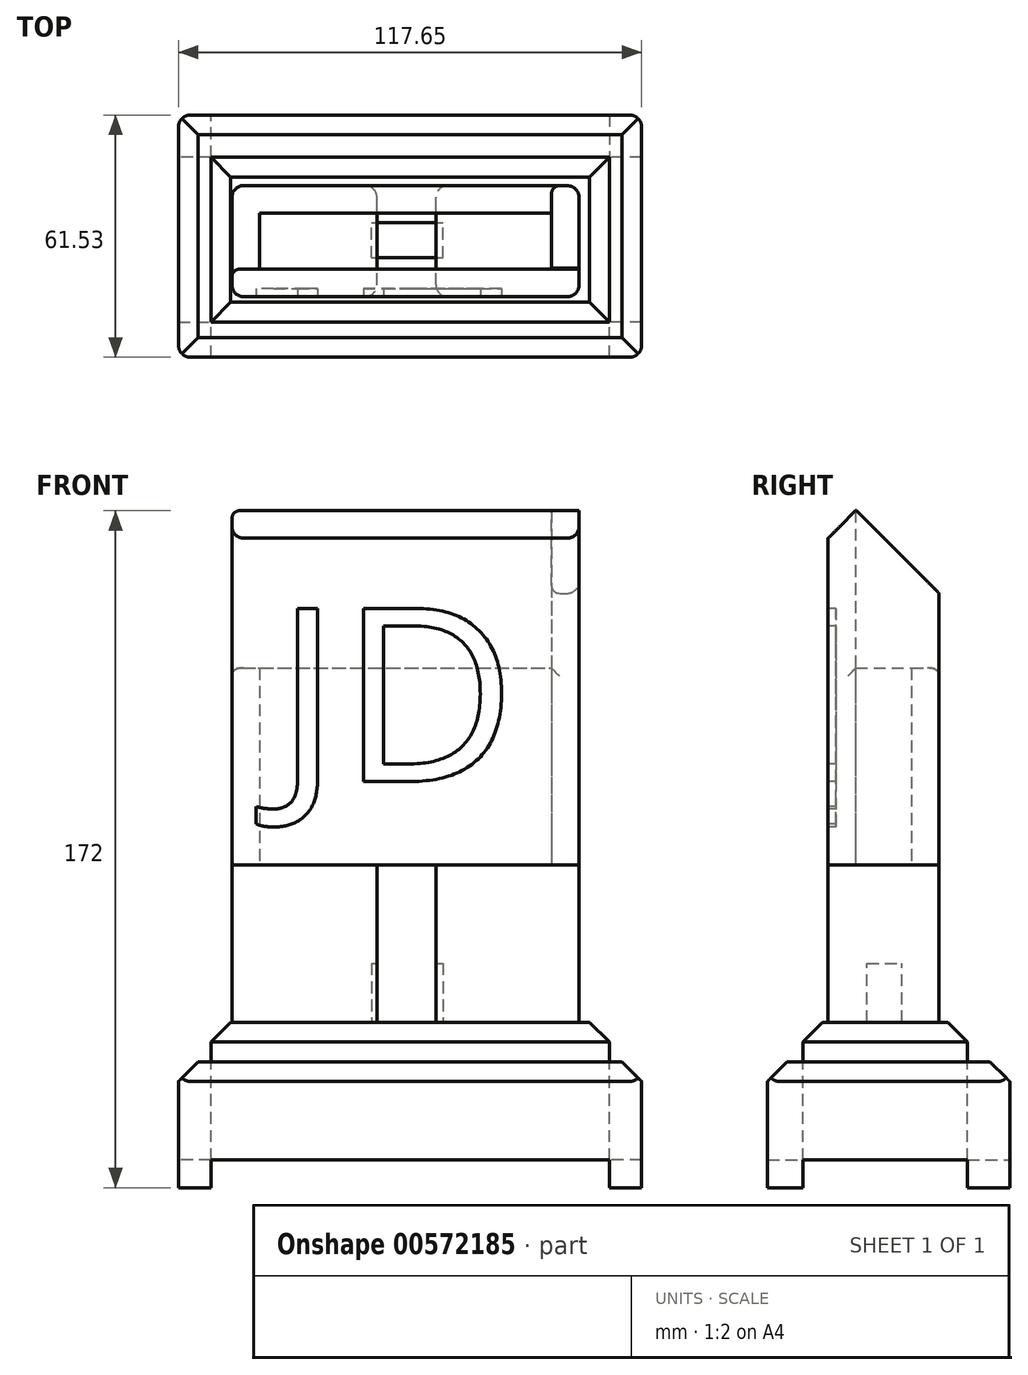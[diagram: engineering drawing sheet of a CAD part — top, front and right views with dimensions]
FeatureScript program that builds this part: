
annotation { "Feature Type Name" : "Feature", "Feature Type Description" : "" }
export const myFeature = defineFeature(function(context is Context, id is Id, definition is map)
    precondition{}
    {
        {
            var Q0;
            Q0=qCreatedBy(makeId("Top.planeOp"),FACE);
            var sketch = newSketch(context, id + "F0", { "sketchPlane" : qUnion([Q0])});
            skLineSegment(sketch, "E0.bottom", {"start": v(-33.87, 3.16) * mm, "end": v(33.23, 3.16) * mm});
            skLineSegment(sketch, "E0.top", {"start": v(-33.87, -3.94) * mm, "end": v(33.23, -3.94) * mm});
            skLineSegment(sketch, "E0.left", {"start": v(-33.87, 3.16) * mm, "end": v(-33.87, -3.94) * mm});
            skLineSegment(sketch, "E0.right", {"start": v(33.23, 3.16) * mm, "end": v(33.23, -3.94) * mm});
            skSolve(sketch);
        }
        {
            var Q0;
            Q0=makeQuery(id+"F0.imprint","IMPRINT",FACE,{"disambiguationData":[TD([[makeQuery(id+"F0.imprint","IMPRINT",EDGE,{"derivedFrom":sQuery(id+"F0.wireOp",EDGE,"E0.bottom")}),-1.0]])]});
            extrude(context, id + "F1", {"entities" : qUnion([Q0]), "depth" : 138.3 * mm, "offsetDistance" : 25 * mm});
        }
        {
            var Q0;
            Q0=qCreatedBy(makeId("Top.planeOp"),FACE);
            var sketch = newSketch(context, id + "F2", { "sketchPlane" : qUnion([Q0])});
            skLineSegment(sketch, "E1.bottom", {"start": v(-37.47, -7.59) * mm, "end": v(36.73, -7.59) * mm});
            skLineSegment(sketch, "E1.top", {"start": v(-37.47, 6.61) * mm, "end": v(36.73, 6.61) * mm});
            skLineSegment(sketch, "E1.left", {"start": v(-37.47, -7.59) * mm, "end": v(-37.47, 6.61) * mm});
            skLineSegment(sketch, "E1.right", {"start": v(36.73, -7.59) * mm, "end": v(36.73, 6.61) * mm});
            skLineSegment(sketch, "E2.0", {"start": v(-44.47, -14.59) * mm, "end": v(43.73, -14.59) * mm});
            skLineSegment(sketch, "E2.1", {"start": v(-44.47, -14.59) * mm, "end": v(-44.47, 13.61) * mm});
            skLineSegment(sketch, "E2.2", {"start": v(-44.47, 13.61) * mm, "end": v(43.73, 13.61) * mm});
            skLineSegment(sketch, "E2.3", {"start": v(43.73, -14.59) * mm, "end": v(43.73, 13.61) * mm});
            skSolve(sketch);
        }
        {
            var Q0;
            Q0=makeQuery(id+"F2.imprint","IMPRINT",FACE,{"disambiguationData":[TD([[makeQuery(id+"F2.imprint","IMPRINT",EDGE,{"derivedFrom":sQuery(id+"F2.wireOp",EDGE,"E1.bottom")}),-1.0]])]});
            extrude(context, id + "F3", {"entities" : qUnion([Q0]), "depth" : 50 * mm, "offsetDistance" : 25 * mm});
        }
        {
            var Q0;
            Q0=makeQuery(id+"F3.opExtrude","CAP_FACE",FACE,{"disambiguationData":[OSD([sQuery(id+"F2.wireOp",EDGE,"E1.bottom"),sQuery(id+"F2.wireOp",EDGE,"E1.top"),sQuery(id+"F2.wireOp",EDGE,"E1.left"),sQuery(id+"F2.wireOp",EDGE,"E1.right"),sQuery(id+"F2.wireOp",EDGE,"E2.0"),sQuery(id+"F2.wireOp",EDGE,"E2.1"),sQuery(id+"F2.wireOp",EDGE,"E2.2"),sQuery(id+"F2.wireOp",EDGE,"E2.3")])],"isStart":true});
            var sketch = newSketch(context, id + "F4", { "sketchPlane" : qUnion([Q0])});
            skLineSegment(sketch, "E3.bottom", {"start": v(-44.47, 14.59) * mm, "end": v(-7.62, 14.59) * mm});
            skLineSegment(sketch, "E3.top", {"start": v(-44.47, -13.61) * mm, "end": v(-7.62, -13.61) * mm});
            skLineSegment(sketch, "E3.left", {"start": v(-44.47, 14.59) * mm, "end": v(-44.47, -13.61) * mm});
            skLineSegment(sketch, "E3.right", {"start": v(-7.62, 14.59) * mm, "end": v(-7.62, -13.61) * mm});
            skLineSegment(sketch, "E4.bottom", {"start": v(7.38, 14.59) * mm, "end": v(43.73, 14.59) * mm});
            skLineSegment(sketch, "E4.top", {"start": v(7.38, -13.61) * mm, "end": v(43.73, -13.61) * mm});
            skLineSegment(sketch, "E4.left", {"start": v(7.38, 14.59) * mm, "end": v(7.38, -13.61) * mm});
            skLineSegment(sketch, "E4.right", {"start": v(43.73, 14.59) * mm, "end": v(43.73, -13.61) * mm});
            skSolve(sketch);
        }
        {
            var Q0;
            Q0 = qSketchRegion(id + "F4", true);
            extrude(context, id + "F5", {"entities" : qUnion([Q0]), "depth" : 40 * mm, "offsetDistance" : 25 * mm});
        }
        {
            var Q0;
            Q0=makeQuery(id+"F5.opExtrude","CAP_FACE",FACE,{"disambiguationData":[OSD([sQuery(id+"F4.wireOp",EDGE,"E3.bottom"),sQuery(id+"F4.wireOp",EDGE,"E3.top"),sQuery(id+"F4.wireOp",EDGE,"E3.left"),sQuery(id+"F4.wireOp",EDGE,"E3.right")])],"isStart":false});
            var sketch = newSketch(context, id + "F6", { "sketchPlane" : qUnion([Q0])});
            skLineSegment(sketch, "E5.bottom", {"start": v(-49.78, 21) * mm, "end": v(51.43, 21) * mm});
            skLineSegment(sketch, "E5.top", {"start": v(-49.78, -20.82) * mm, "end": v(51.43, -20.82) * mm});
            skLineSegment(sketch, "E5.left", {"start": v(-49.78, 21) * mm, "end": v(-49.78, -20.82) * mm});
            skLineSegment(sketch, "E5.right", {"start": v(51.43, 21) * mm, "end": v(51.43, -20.82) * mm});
            skSolve(sketch);
        }
        {
            var Q0;
            Q0 = qSketchRegion(id + "F6", true);
            extrude(context, id + "F7", {"entities" : qUnion([Q0]), "depth" : 10 * mm, "offsetDistance" : 25 * mm});
        }
        {
            var Q0;
            Q0=makeQuery(id+"F7.opExtrude","CAP_FACE",FACE,{"disambiguationData":[OSD([sQuery(id+"F6.wireOp",EDGE,"E5.bottom"),sQuery(id+"F6.wireOp",EDGE,"E5.top"),sQuery(id+"F6.wireOp",EDGE,"E5.left"),sQuery(id+"F6.wireOp",EDGE,"E5.right")])],"isStart":false});
            var sketch = newSketch(context, id + "F8", { "sketchPlane" : qUnion([Q0])});
            skLineSegment(sketch, "E6.bottom", {"start": v(-8.93, 4.69) * mm, "end": v(9.19, 4.69) * mm});
            skLineSegment(sketch, "E6.top", {"start": v(-8.93, -4.18) * mm, "end": v(9.19, -4.18) * mm});
            skLineSegment(sketch, "E6.left", {"start": v(-8.93, 4.69) * mm, "end": v(-8.93, -4.18) * mm});
            skLineSegment(sketch, "E6.right", {"start": v(9.19, 4.69) * mm, "end": v(9.19, -4.18) * mm});
            skSolve(sketch);
        }
        {
            var Q0;
            Q0 = qSketchRegion(id + "F8", true);
            extrude(context, id + "F9", {"entities" : qUnion([Q0]), "operationType" : NewBodyOperationType.REMOVE, "oppositeDirection" : true, "depth" : 25 * mm, "offsetDistance" : 25 * mm});
        }
        {
            var Q0;
            Q0=makeQuery(id+"F7.opExtrude","CAP_FACE",FACE,{"disambiguationData":[OSD([sQuery(id+"F6.wireOp",EDGE,"E5.bottom"),sQuery(id+"F6.wireOp",EDGE,"E5.top"),sQuery(id+"F6.wireOp",EDGE,"E5.left"),sQuery(id+"F6.wireOp",EDGE,"E5.right")])],"isStart":false});
            var sketch = newSketch(context, id + "F10", { "sketchPlane" : qUnion([Q0])});
            skLineSegment(sketch, "E7.bottom", {"start": v(-58.03, 29.97) * mm, "end": v(59.62, 29.97) * mm});
            skLineSegment(sketch, "E7.top", {"start": v(-58.03, -31.56) * mm, "end": v(59.62, -31.56) * mm});
            skLineSegment(sketch, "E7.left", {"start": v(-58.03, 29.97) * mm, "end": v(-58.03, -31.56) * mm});
            skLineSegment(sketch, "E7.right", {"start": v(59.62, 29.97) * mm, "end": v(59.62, -31.56) * mm});
            skSolve(sketch);
        }
        {
            var Q0;
            Q0=makeQuery(id+"F10.imprint","IMPRINT",FACE,{"disambiguationData":[TD([[makeQuery(id+"F10.imprint","IMPRINT",EDGE,{"derivedFrom":sQuery(id+"F10.wireOp",EDGE,"E7.bottom")}),-1.0]])]});
            extrude(context, id + "F11", {"entities" : qUnion([Q0]), "depth" : 25 * mm, "offsetDistance" : 25 * mm});
        }
        {
            var Q0;
            Q0=makeQuery(id+"F3.opExtrude","CAP_FACE",FACE,{"disambiguationData":[OSD([sQuery(id+"F2.wireOp",EDGE,"E1.bottom"),sQuery(id+"F2.wireOp",EDGE,"E1.top"),sQuery(id+"F2.wireOp",EDGE,"E1.left"),sQuery(id+"F2.wireOp",EDGE,"E1.right"),sQuery(id+"F2.wireOp",EDGE,"E2.0"),sQuery(id+"F2.wireOp",EDGE,"E2.1"),sQuery(id+"F2.wireOp",EDGE,"E2.2"),sQuery(id+"F2.wireOp",EDGE,"E2.3")])],"isStart":false});
            var sketch = newSketch(context, id + "F12", { "sketchPlane" : qUnion([Q0])});
            skLineSegment(sketch, "E8.bottom", {"start": v(-44.47, -7.59) * mm, "end": v(43.73, -7.59) * mm});
            skLineSegment(sketch, "E8.top", {"start": v(-44.47, -14.59) * mm, "end": v(43.73, -14.59) * mm});
            skLineSegment(sketch, "E8.left", {"start": v(-44.47, -7.59) * mm, "end": v(-44.47, -14.59) * mm});
            skLineSegment(sketch, "E8.right", {"start": v(43.73, -7.59) * mm, "end": v(43.73, -14.59) * mm});
            skLineSegment(sketch, "E9.bottom", {"start": v(36.73, 13.61) * mm, "end": v(43.73, 13.61) * mm});
            skLineSegment(sketch, "E9.top", {"start": v(36.73, -7.59) * mm, "end": v(43.73, -7.59) * mm});
            skLineSegment(sketch, "E9.left", {"start": v(36.73, 13.61) * mm, "end": v(36.73, -7.59) * mm});
            skLineSegment(sketch, "E9.right", {"start": v(43.73, 13.61) * mm, "end": v(43.73, -7.59) * mm});
            skSolve(sketch);
        }
        {
            var Q0;
            Q0 = qSketchRegion(id + "F12", true);
            extrude(context, id + "F13", {"entities" : qUnion([Q0]), "operationType" : NewBodyOperationType.ADD, "depth" : 40 * mm, "offsetDistance" : 25 * mm});
        }
        {
            var Q0;
            Q0=makeQuery(id+"F13.opExtrude","CAP_EDGE",EDGE,{"disambiguationData":[OSD([sQuery(id+"F12.wireOp",EDGE,"E9.bottom")])],"isStart":false});
            chamfer(context, id + "F14", {"entities" : qUnion([Q0]), "width" : 21 * mm, "tangentPropagation" : true});
        }
        {
            var Q0;
            Q0=makeQuery(id+"F13.opExtrude","CAP_EDGE",EDGE,{"disambiguationData":[OSD([sQuery(id+"F12.wireOp",EDGE,"E8.top")])],"isStart":false});
            chamfer(context, id + "F15", {"entities" : qUnion([Q0]), "width" : 7 * mm, "tangentPropagation" : true});
        }
        {
            var Q0;
            Q0=makeQuery(id+"F3.opExtrude","SWEPT_EDGE",EDGE,{"disambiguationData":[OSD([sQuery(id+"F2.wireOp",EDGE,"E2.1"),sQuery(id+"F2.wireOp",EDGE,"E2.2")])]});
            fillet(context, id + "F16", {"entities" : qUnion([Q0]), "radius" : 3 * mm, "tangentPropagation" : true, "allowEdgeOverflow" : false});
        }
        {
            var Q0;
            Q0=makeQuery(id+"F13.boolean.opBoolean","MERGE",EDGE,{"derivedFrom":[makeQuery(id+"F3.opExtrude","SWEPT_EDGE",EDGE,{"disambiguationData":[OSD([sQuery(id+"F2.wireOp",EDGE,"E2.2"),sQuery(id+"F2.wireOp",EDGE,"E2.3")])]}),makeQuery(id+"F13.opExtrude","SWEPT_EDGE",EDGE,{"disambiguationData":[OSD([sQuery(id+"F12.wireOp",EDGE,"E9.bottom"),sQuery(id+"F12.wireOp",EDGE,"E9.right")])]})]});
            fillet(context, id + "F17", {"entities" : qUnion([Q0]), "radius" : 3 * mm, "tangentPropagation" : true, "allowEdgeOverflow" : false});
        }
        {
            var Q0;
            Q0=makeQuery(id+"F5.opExtrude","SWEPT_EDGE",EDGE,{"disambiguationData":[OSD([sQuery(id+"F4.wireOp",EDGE,"E4.top"),sQuery(id+"F4.wireOp",EDGE,"E4.right")])]});
            var Q1;
            Q1=makeQuery(id+"F5.opExtrude","SWEPT_EDGE",EDGE,{"disambiguationData":[OSD([sQuery(id+"F4.wireOp",EDGE,"E3.top"),sQuery(id+"F4.wireOp",EDGE,"E3.left")])]});
            fillet(context, id + "F18", {"entities" : qUnion([Q0, Q1]), "radius" : 3 * mm, "tangentPropagation" : true, "allowEdgeOverflow" : false});
        }
        {
            var Q0;
            Q0=makeQuery(id+"F13.boolean.opBoolean","MERGE",EDGE,{"derivedFrom":[makeQuery(id+"F3.opExtrude","SWEPT_EDGE",EDGE,{"disambiguationData":[OSD([sQuery(id+"F2.wireOp",EDGE,"E2.0"),sQuery(id+"F2.wireOp",EDGE,"E2.3")])]}),makeQuery(id+"F13.opExtrude","SWEPT_EDGE",EDGE,{"disambiguationData":[OSD([sQuery(id+"F12.wireOp",EDGE,"E8.top"),sQuery(id+"F12.wireOp",EDGE,"E8.right")])]})]});
            var Q1;
            Q1=makeQuery(id+"F5.opExtrude","SWEPT_EDGE",EDGE,{"disambiguationData":[OSD([sQuery(id+"F4.wireOp",EDGE,"E4.bottom"),sQuery(id+"F4.wireOp",EDGE,"E4.right")])]});
            fillet(context, id + "F19", {"entities" : qUnion([Q0, Q1]), "radius" : 3 * mm, "tangentPropagation" : true, "allowEdgeOverflow" : false});
        }
        {
            var Q0;
            Q0=makeQuery(id+"F13.boolean.opBoolean","MERGE",EDGE,{"derivedFrom":[makeQuery(id+"F3.opExtrude","SWEPT_EDGE",EDGE,{"disambiguationData":[OSD([sQuery(id+"F2.wireOp",EDGE,"E2.0"),sQuery(id+"F2.wireOp",EDGE,"E2.1")])]}),makeQuery(id+"F13.opExtrude","SWEPT_EDGE",EDGE,{"disambiguationData":[OSD([sQuery(id+"F12.wireOp",EDGE,"E8.top"),sQuery(id+"F12.wireOp",EDGE,"E8.left")])]})]});
            var Q1;
            Q1=makeQuery(id+"F5.opExtrude","SWEPT_EDGE",EDGE,{"disambiguationData":[OSD([sQuery(id+"F4.wireOp",EDGE,"E3.bottom"),sQuery(id+"F4.wireOp",EDGE,"E3.left")])]});
            fillet(context, id + "F20", {"entities" : qUnion([Q0, Q1]), "radius" : 3 * mm, "tangentPropagation" : true, "allowEdgeOverflow" : false});
        }
        {
            var Q0;
            Q0=makeQuery(id+"F7.opExtrude","CAP_EDGE",EDGE,{"disambiguationData":[OSD([sQuery(id+"F6.wireOp",EDGE,"E5.top")])],"isStart":true});
            chamfer(context, id + "F21", {"entities" : qUnion([Q0]), "width" : 5 * mm, "tangentPropagation" : true});
        }
        {
            var Q0;
            Q0=makeQuery(id+"F7.opExtrude","CAP_EDGE",EDGE,{"disambiguationData":[OSD([sQuery(id+"F6.wireOp",EDGE,"E5.left")])],"isStart":true});
            chamfer(context, id + "F22", {"entities" : qUnion([Q0]), "width" : 5 * mm, "tangentPropagation" : true});
        }
        {
            var Q0;
            Q0=makeQuery(id+"F7.opExtrude","CAP_EDGE",EDGE,{"disambiguationData":[OSD([sQuery(id+"F6.wireOp",EDGE,"E5.right")])],"isStart":true});
            chamfer(context, id + "F23", {"entities" : qUnion([Q0]), "width" : 5 * mm, "tangentPropagation" : true});
        }
        {
            var Q0;
            Q0=makeQuery(id+"F7.opExtrude","CAP_EDGE",EDGE,{"disambiguationData":[OSD([sQuery(id+"F6.wireOp",EDGE,"E5.bottom")])],"isStart":true});
            chamfer(context, id + "F24", {"entities" : qUnion([Q0]), "width" : 5 * mm, "tangentPropagation" : true});
        }
        {
            var Q0;
            Q0=makeQuery(id+"F11.opExtrude","CAP_EDGE",EDGE,{"disambiguationData":[OSD([sQuery(id+"F10.wireOp",EDGE,"E7.top")])],"isStart":true});
            chamfer(context, id + "F25", {"entities" : qUnion([Q0]), "width" : 5 * mm, "tangentPropagation" : true});
        }
        {
            var Q0;
            Q0=makeQuery(id+"F11.opExtrude","CAP_EDGE",EDGE,{"disambiguationData":[OSD([sQuery(id+"F10.wireOp",EDGE,"E7.right")])],"isStart":true});
            var Q1;
            Q1=makeQuery(id+"F11.opExtrude","CAP_EDGE",EDGE,{"disambiguationData":[OSD([sQuery(id+"F10.wireOp",EDGE,"E7.bottom")])],"isStart":true});
            chamfer(context, id + "F26", {"entities" : qUnion([Q0, Q1]), "width" : 5 * mm, "tangentPropagation" : true});
        }
        {
            var Q0;
            Q0=makeQuery(id+"F11.opExtrude","CAP_EDGE",EDGE,{"disambiguationData":[OSD([sQuery(id+"F10.wireOp",EDGE,"E7.left")])],"isStart":true});
            chamfer(context, id + "F27", {"entities" : qUnion([Q0]), "width" : 5 * mm, "tangentPropagation" : true});
        }
        {
            var Q0;
            Q0=makeQuery(id+"F5.opExtrude","SWEPT_EDGE",EDGE,{"disambiguationData":[OSD([sQuery(id+"F2.wireOp",EDGE,"E2.2"),sQuery(id+"F4.wireOp",EDGE,"E3.top"),sQuery(id+"F4.wireOp",EDGE,"E3.right")])]});
            var Q1;
            Q1=makeQuery(id+"F5.opExtrude","SWEPT_EDGE",EDGE,{"disambiguationData":[OSD([sQuery(id+"F2.wireOp",EDGE,"E2.0"),sQuery(id+"F4.wireOp",EDGE,"E3.bottom"),sQuery(id+"F4.wireOp",EDGE,"E3.right")])]});
            var Q2;
            Q2=makeQuery(id+"F5.opExtrude","SWEPT_EDGE",EDGE,{"disambiguationData":[OSD([sQuery(id+"F2.wireOp",EDGE,"E2.0"),sQuery(id+"F4.wireOp",EDGE,"E4.bottom"),sQuery(id+"F4.wireOp",EDGE,"E4.left")])]});
            var Q3;
            Q3=makeQuery(id+"F5.opExtrude","SWEPT_EDGE",EDGE,{"disambiguationData":[OSD([sQuery(id+"F2.wireOp",EDGE,"E2.2"),sQuery(id+"F4.wireOp",EDGE,"E4.top"),sQuery(id+"F4.wireOp",EDGE,"E4.left")])]});
            fillet(context, id + "F28", {"entities" : qUnion([Q0, Q1, Q2, Q3]), "radius" : 3 * mm, "tangentPropagation" : true, "allowEdgeOverflow" : false});
        }
        {
            var Q0;
            Q0=makeQuery(id+"F3.opExtrude","CAP_EDGE",EDGE,{"disambiguationData":[OSD([sQuery(id+"F2.wireOp",EDGE,"E2.2")])],"isStart":false});
            fillet(context, id + "F29", {"entities" : qUnion([Q0]), "radius" : 2 * mm, "tangentPropagation" : true, "allowEdgeOverflow" : false});
        }
        {
            var Q0;
            Q0=makeQuery(id+"F13.opExtrude","SWEPT_EDGE",EDGE,{"disambiguationData":[OSD([sQuery(id+"F2.wireOp",EDGE,"E2.1"),sQuery(id+"F12.wireOp",EDGE,"E8.bottom"),sQuery(id+"F12.wireOp",EDGE,"E8.left")])]});
            fillet(context, id + "F30", {"entities" : qUnion([Q0]), "radius" : 2 * mm, "tangentPropagation" : true, "allowEdgeOverflow" : false});
        }
        {
            var Q0;
            Q0=makeQuery(id+"F13.opExtrude","SWEPT_EDGE",EDGE,{"disambiguationData":[OSD([sQuery(id+"F2.wireOp",EDGE,"E2.2"),sQuery(id+"F12.wireOp",EDGE,"E9.bottom"),sQuery(id+"F12.wireOp",EDGE,"E9.left")])]});
            fillet(context, id + "F31", {"entities" : qUnion([Q0]), "radius" : 2 * mm, "tangentPropagation" : true, "allowEdgeOverflow" : false});
        }
        {
            var Q0;
            Q0=makeQuery(id+"F11.opExtrude","CAP_FACE",FACE,{"disambiguationData":[OSD([sQuery(id+"F6.wireOp",EDGE,"E5.bottom"),sQuery(id+"F6.wireOp",EDGE,"E5.top"),sQuery(id+"F6.wireOp",EDGE,"E5.left"),sQuery(id+"F6.wireOp",EDGE,"E5.right"),sQuery(id+"F10.wireOp",EDGE,"E7.bottom"),sQuery(id+"F10.wireOp",EDGE,"E7.top"),sQuery(id+"F10.wireOp",EDGE,"E7.left"),sQuery(id+"F10.wireOp",EDGE,"E7.right")])],"isStart":false});
            var sketch = newSketch(context, id + "F32", { "sketchPlane" : qUnion([Q0])});
            skLineSegment(sketch, "E10.bottom", {"start": v(-58.03, 29.97) * mm, "end": v(-49.78, 29.97) * mm});
            skLineSegment(sketch, "E10.top", {"start": v(-58.03, 21) * mm, "end": v(-49.78, 21) * mm});
            skLineSegment(sketch, "E10.left", {"start": v(-58.03, 29.97) * mm, "end": v(-58.03, 21) * mm});
            skLineSegment(sketch, "E10.right", {"start": v(-49.78, 29.97) * mm, "end": v(-49.78, 21) * mm});
            skLineSegment(sketch, "E11.bottom", {"start": v(59.62, 29.97) * mm, "end": v(51.43, 29.97) * mm});
            skLineSegment(sketch, "E11.top", {"start": v(59.62, 21) * mm, "end": v(51.43, 21) * mm});
            skLineSegment(sketch, "E11.left", {"start": v(59.62, 29.97) * mm, "end": v(59.62, 21) * mm});
            skLineSegment(sketch, "E11.right", {"start": v(51.43, 29.97) * mm, "end": v(51.43, 21) * mm});
            skLineSegment(sketch, "E12.bottom", {"start": v(59.62, -31.56) * mm, "end": v(51.43, -31.56) * mm});
            skLineSegment(sketch, "E12.top", {"start": v(59.62, -20.82) * mm, "end": v(51.43, -20.82) * mm});
            skLineSegment(sketch, "E12.left", {"start": v(59.62, -31.56) * mm, "end": v(59.62, -20.82) * mm});
            skLineSegment(sketch, "E12.right", {"start": v(51.43, -31.56) * mm, "end": v(51.43, -20.82) * mm});
            skLineSegment(sketch, "E13.bottom", {"start": v(-49.78, -20.82) * mm, "end": v(-58.03, -20.82) * mm});
            skLineSegment(sketch, "E13.top", {"start": v(-49.78, -31.56) * mm, "end": v(-58.03, -31.56) * mm});
            skLineSegment(sketch, "E13.left", {"start": v(-49.78, -20.82) * mm, "end": v(-49.78, -31.56) * mm});
            skLineSegment(sketch, "E13.right", {"start": v(-58.03, -20.82) * mm, "end": v(-58.03, -31.56) * mm});
            skSolve(sketch);
        }
        {
            var Q0;
            Q0=makeQuery(id+"F32.imprint","IMPRINT",FACE,{"disambiguationData":[TD([[makeQuery(id+"F32.imprint","IMPRINT",EDGE,{"derivedFrom":sQuery(id+"F32.wireOp",EDGE,"E10.bottom")}),-1.0]])]});
            var Q1;
            Q1=makeQuery(id+"F32.imprint","IMPRINT",FACE,{"disambiguationData":[TD([[makeQuery(id+"F32.imprint","IMPRINT",EDGE,{"derivedFrom":sQuery(id+"F32.wireOp",EDGE,"E13.bottom")}),1.0]])]});
            var Q2;
            Q2 = qSketchRegion(id + "F32", true);
            extrude(context, id + "F33", {"entities" : qUnion([Q0, Q1, Q2]), "operationType" : NewBodyOperationType.ADD, "depth" : 7 * mm, "offsetDistance" : 25 * mm});
        }
        {
            var Q0;
            Q0=makeQuery(id+"F33.boolean.opBoolean","MERGE",EDGE,{"derivedFrom":[makeQuery(id+"F11.opExtrude","SWEPT_EDGE",EDGE,{"disambiguationData":[OSD([sQuery(id+"F10.wireOp",EDGE,"E7.top"),sQuery(id+"F10.wireOp",EDGE,"E7.left")])]}),makeQuery(id+"F33.opExtrude","SWEPT_EDGE",EDGE,{"disambiguationData":[OSD([sQuery(id+"F32.wireOp",EDGE,"E13.top"),sQuery(id+"F32.wireOp",EDGE,"E13.right")])]})]});
            var Q1;
            Q1=makeQuery(id+"F33.boolean.opBoolean","MERGE",EDGE,{"derivedFrom":[makeQuery(id+"F11.opExtrude","SWEPT_EDGE",EDGE,{"disambiguationData":[OSD([sQuery(id+"F10.wireOp",EDGE,"E7.bottom"),sQuery(id+"F10.wireOp",EDGE,"E7.left")])]}),makeQuery(id+"F33.opExtrude","SWEPT_EDGE",EDGE,{"disambiguationData":[OSD([sQuery(id+"F32.wireOp",EDGE,"E10.bottom"),sQuery(id+"F32.wireOp",EDGE,"E10.left")])]})]});
            var Q2;
            Q2=makeQuery(id+"F33.boolean.opBoolean","MERGE",EDGE,{"derivedFrom":[makeQuery(id+"F11.opExtrude","SWEPT_EDGE",EDGE,{"disambiguationData":[OSD([sQuery(id+"F10.wireOp",EDGE,"E7.top"),sQuery(id+"F10.wireOp",EDGE,"E7.right")])]}),makeQuery(id+"F33.opExtrude","SWEPT_EDGE",EDGE,{"disambiguationData":[OSD([sQuery(id+"F32.wireOp",EDGE,"E12.bottom"),sQuery(id+"F32.wireOp",EDGE,"E12.left")])]})]});
            var Q3;
            Q3=makeQuery(id+"F33.boolean.opBoolean","MERGE",EDGE,{"derivedFrom":[makeQuery(id+"F11.opExtrude","SWEPT_EDGE",EDGE,{"disambiguationData":[OSD([sQuery(id+"F10.wireOp",EDGE,"E7.bottom"),sQuery(id+"F10.wireOp",EDGE,"E7.right")])]}),makeQuery(id+"F33.opExtrude","SWEPT_EDGE",EDGE,{"disambiguationData":[OSD([sQuery(id+"F32.wireOp",EDGE,"E11.bottom"),sQuery(id+"F32.wireOp",EDGE,"E11.left")])]})]});
            fillet(context, id + "F34", {"entities" : qUnion([Q0, Q1, Q2, Q3]), "radius" : 3 * mm, "tangentPropagation" : true, "allowEdgeOverflow" : false});
        }
        {
            var Q0;
            Q0=makeQuery(id+"F1.opExtrude","SWEPT_BODY",BODY,{"disambiguationData":[OSD([sQuery(id+"F0.wireOp",EDGE,"E0.bottom"),sQuery(id+"F0.wireOp",EDGE,"E0.top"),sQuery(id+"F0.wireOp",EDGE,"E0.left"),sQuery(id+"F0.wireOp",EDGE,"E0.right")])]});
            deleteBodies(context, id + "F35", {"entities" : qUnion([Q0])});
        }
        {
            var Q0;
            Q0=makeQuery(id+"F13.boolean.opBoolean","MERGE",FACE,{"derivedFrom":[makeQuery(id+"F3.opExtrude","SWEPT_FACE",FACE,{"disambiguationData":[OSD([sQuery(id+"F2.wireOp",EDGE,"E2.0")])]}),makeQuery(id+"F13.opExtrude","SWEPT_FACE",FACE,{"disambiguationData":[OSD([sQuery(id+"F12.wireOp",EDGE,"E8.top")])]})]});
            var sketch = newSketch(context, id + "F36", { "sketchPlane" : qUnion([Q0])});
            skText(sketch, "E14", { "text": "JD\n", "fontName": "OpenSans-Regular.ttf"});
            const initialGuessF36  = {"E14": [-0.03352, 0.02122, 1, 0, 0.04433]};
            skSetInitialGuess(sketch, initialGuessF36);
            skSolve(sketch);
        }
        {
            var Q0;
            Q0 = qSketchRegion(id + "F36", true);
            extrude(context, id + "F37", {"entities" : qUnion([Q0]), "operationType" : NewBodyOperationType.REMOVE, "oppositeDirection" : true, "depth" : 2 * mm, "offsetDistance" : 25 * mm});
        }
    });
